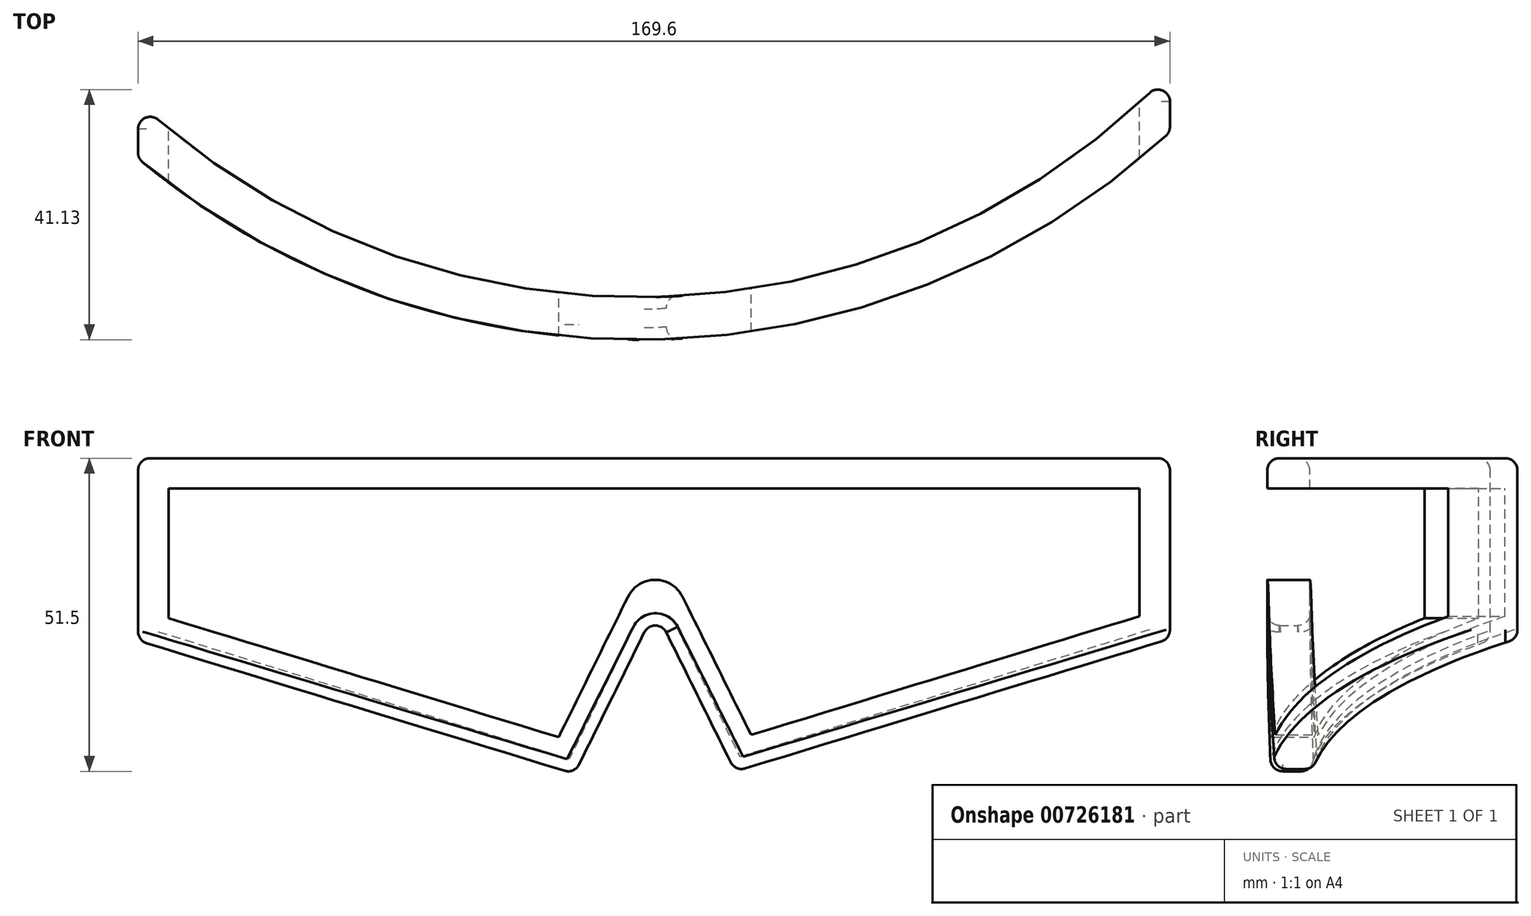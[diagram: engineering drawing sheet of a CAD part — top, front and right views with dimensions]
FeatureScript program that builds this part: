
annotation { "Feature Type Name" : "Feature", "Feature Type Description" : "" }
export const myFeature = defineFeature(function(context is Context, id is Id, definition is map)
    precondition{}
    {
        {
            var Q0;
            Q0=qCreatedBy(makeId("Front.planeOp"),FACE);
            var sketch = newSketch(context, id + "F0", { "sketchPlane" : qUnion([Q0])});
            skLineSegment(sketch, "E0.top", {"start": v(-14.32, 57.35) * mm, "end": v(-99.32, 57.35) * mm});
            skLineSegment(sketch, "E0.right", {"start": v(-99.32, 27.35) * mm, "end": v(-99.32, 57.35) * mm});
            skLineSegment(sketch, "E1", {"start": v(-27.59, 5.44) * mm, "end": v(-14.32, 32.35) * mm});
            skLineSegment(sketch, "E2", {"start": v(-27.59, 5.44) * mm, "end": v(-99.32, 27.35) * mm});
            skLineSegment(sketch, "E3.MirrorCS", {"start": v(-1.16, 5.82) * mm, "end": v(70.28, 27.64) * mm});
            skLineSegment(sketch, "E4.MirrorCS", {"start": v(70.28, 27.64) * mm, "end": v(70.28, 57.35) * mm});
            skLineSegment(sketch, "E5.MirrorCS", {"start": v(-14.32, 57.35) * mm, "end": v(70.28, 57.35) * mm});
            skLineSegment(sketch, "E6.MirrorCS", {"start": v(-1.16, 5.82) * mm, "end": v(-14.32, 32.35) * mm});
            skSolve(sketch);
        }
        {
            var Q0;
            Q0=qSketchRegion(id+"F0",true);
            extrude(context, id + "F1", {"entities" : qUnion([Q0]), "depth" : 150 * mm, "offsetDistance" : 25 * mm});
        }
        {
            var Q0;
            Q0=qCreatedBy(makeId("Front.planeOp"),FACE);
            var sketch = newSketch(context, id + "F2", { "sketchPlane" : qUnion([Q0])});
            skLineSegment(sketch, "E7.0", {"start": v(65.28, 31.34) * mm, "end": v(1.43, 11.84) * mm});
            skLineSegment(sketch, "E7.1", {"start": v(65.28, 52.35) * mm, "end": v(65.28, 31.34) * mm});
            skLineSegment(sketch, "E7.2", {"start": v(-14.33, 43.62) * mm, "end": v(-30.2, 11.46) * mm});
            skLineSegment(sketch, "E7.3", {"start": v(-30.2, 11.46) * mm, "end": v(-94.32, 31.05) * mm});
            skLineSegment(sketch, "E7.4", {"start": v(-94.32, 31.05) * mm, "end": v(-94.32, 52.35) * mm});
            skLineSegment(sketch, "E7.5", {"start": v(1.43, 11.84) * mm, "end": v(-14.33, 43.62) * mm});
            skLineSegment(sketch, "E7.6", {"start": v(-94.32, 52.35) * mm, "end": v(65.28, 52.35) * mm});
            skSolve(sketch);
        }
        {
            var Q0;
            Q0=qSketchRegion(id+"F2",true);
            extrude(context, id + "F3", {"entities" : qUnion([Q0]), "operationType" : NewBodyOperationType.REMOVE, "depth" : 200 * mm, "offsetDistance" : 25 * mm});
        }
        {
            var Q0;
            Q0=makeQuery(id+"F1.opExtrude","SWEPT_FACE",FACE,{"disambiguationData":[OSD([sQuery(id+"F0.wireOp",EDGE,"E0.top"),sQuery(id+"F0.wireOp",EDGE,"E5.MirrorCS")])]});
            var sketch = newSketch(context, id + "F4", { "sketchPlane" : qUnion([Q0])});
            skArc(sketch, "E8", {"start": v(-139.84, -48.26) * mm, "mid": v(-17.33, -138.81) * mm, "end": v(105.65, -48.9) * mm});
            skArc(sketch, "E9.0", {"start": v(-133.16, -46.2) * mm, "mid": v(-17.31, -131.81) * mm, "end": v(98.98, -46.8) * mm});
            skLineSegment(sketch, "E10", {"start": v(-139.84, -48.26) * mm, "end": v(-133.16, -46.2) * mm});
            skLineSegment(sketch, "E11", {"start": v(98.98, -46.8) * mm, "end": v(105.65, -48.9) * mm});
            skSolve(sketch);
        }
        {
            var Q0;
            Q0=qSketchRegion(id+"F4",true);
            extrude(context, id + "F5", {"entities" : qUnion([Q0]), "operationType" : NewBodyOperationType.INTERSECT, "oppositeDirection" : true, "depth" : 150 * mm, "offsetDistance" : 25 * mm});
        }
        {
            var Q0;
            Q0=makeQuery(id+"F1.opExtrude","SWEPT_FACE",FACE,{"disambiguationData":[OSD([sQuery(id+"F0.wireOp",EDGE,"E0.right")])]});
            var Q1;
            Q1=makeQuery(id+"F1.opExtrude","SWEPT_FACE",FACE,{"disambiguationData":[OSD([sQuery(id+"F0.wireOp",EDGE,"E0.top"),sQuery(id+"F0.wireOp",EDGE,"E5.MirrorCS")])]});
            var Q2;
            Q2=makeQuery(id+"F1.opExtrude","SWEPT_FACE",FACE,{"disambiguationData":[OSD([sQuery(id+"F0.wireOp",EDGE,"E2")])]});
            var Q3;
            Q3=makeQuery(id+"F1.opExtrude","SWEPT_FACE",FACE,{"disambiguationData":[OSD([sQuery(id+"F0.wireOp",EDGE,"E6.MirrorCS")])]});
            var Q4;
            Q4=makeQuery(id+"F1.opExtrude","SWEPT_FACE",FACE,{"disambiguationData":[OSD([sQuery(id+"F0.wireOp",EDGE,"E1")])]});
            var Q5;
            Q5=makeQuery(id+"F1.opExtrude","SWEPT_FACE",FACE,{"disambiguationData":[OSD([sQuery(id+"F0.wireOp",EDGE,"E3.MirrorCS")])]});
            var Q6;
            Q6=makeQuery(id+"F1.opExtrude","SWEPT_FACE",FACE,{"disambiguationData":[OSD([sQuery(id+"F0.wireOp",EDGE,"E4.MirrorCS")])]});
            fillet(context, id + "F6", {"entities" : qUnion([Q0, Q1, Q2, Q3, Q4, Q5, Q6]), "radius" : 2 * mm, "tangentPropagation" : true, "allowEdgeOverflow" : false});
        }
        {
            var Q0;
            Q0=makeQuery(id+"F3.boolean.opBoolean","COPY",EDGE,{"derivedFrom":makeQuery(id+"F3.opExtrude","SWEPT_EDGE",EDGE,{"disambiguationData":[OSD([sQuery(id+"F2.wireOp",EDGE,"E7.2"),sQuery(id+"F2.wireOp",EDGE,"E7.5")])]})});
            fillet(context, id + "F7", {"entities" : qUnion([Q0]), "radius" : 5 * mm, "tangentPropagation" : true, "allowEdgeOverflow" : false});
        }
    });
